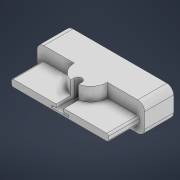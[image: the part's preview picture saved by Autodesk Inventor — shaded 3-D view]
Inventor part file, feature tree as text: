
AUTODESK INVENTOR PART (.ipt)
format: ipt  version: 2022 (Build 260153000, 153)  size: 450,048 bytes
history: native  units: mm
features: sketch x7, extrude x6, fillet x2, emboss x1
ambient origin geometry x8: Origin, YZ Plane, XZ Plane, XY Plane, X Axis, Y Axis, Z Axis, Center Point
bodies: Solid1 (feature_tree)
feature tree (16):
  extrude  "Extrusion1"  Depth=17.0mm
  emboss  "Emboss1"
  extrude  "Extrusion12"  Depth=1.0mm TaperAngle=0.0deg
  extrude  "Extrusion13"  Depth=8.0mm
  extrude  "Extrusion14"  Depth=2.0mm TaperAngle=0.0deg
  extrude  "Extrusion15"  Depth=56.8mm
  fillet  "Fillet6"  Radius=18.0mm
  fillet  "Fillet7"  Radius=1.0mm
  extrude  "Extrusion16"  Depth=4.0mm
  sketch  "Sketch1"  dims[d0=63.0mm d1=17.0mm]
  sketch  "Sketch10"  dims[d2=35.0mm d3=0.0mm d33=1.0mm d34=0.0mm]
  sketch  "Sketch15"  dims[d67=5.0mm d68=8.0mm]
  sketch  "Sketch16"  dims[d69=18.0mm d70=0.0mm d73=2.0mm d74=0.0mm]
  sketch  "Sketch17"  dims[d76=1.0mm d77=0.0mm d78=56.8mm d79=18.0mm d80=0.0mm d81=1.0mm]
  sketch  "Sketch18"  dims[d82=4.0mm d84=19.5mm]
  sketch  "Sketch19"  dims[d85=8.0mm d86=0.0mm d90=8.25mm d91=2.25mm d92=10.0mm d93=10.0mm d51=0.5mm d52=0.872665mm d53=0.5mm d54=0.872665mm]
